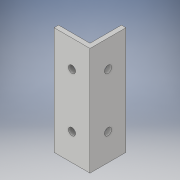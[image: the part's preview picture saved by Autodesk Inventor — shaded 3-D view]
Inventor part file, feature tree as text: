
AUTODESK INVENTOR PART (.ipt)
format: ipt  version: 2018 (Build 220112000, 112)  size: 121,344 bytes
history: native  units: in
note: dims shown in document units (in); Inventor stores cm internally (conversion verified against a paired STEP export)
features: extrude x3, sketch x3
ambient origin geometry x8: Origin, YZ Plane, XZ Plane, XY Plane, X Axis, Y Axis, Z Axis, Center Point
bodies: Solid1 (feature_tree)
feature tree (6):
  extrude  "Extrusion1"  Depth=0.125in
  extrude  "Extrusion2"  Depth=0.125in
  extrude  "Extrusion3"  Depth=1.0in
  sketch  "Sketch1"  dims[d0=1.0in d1=0.125in]
  sketch  "Sketch2"  dims[d2=1.0in d3=0.125in]
  sketch  "Sketch3"  dims[d4=3.0in d5=0.0in d6=0.5in d7=0.75in d8=0.75in d9=0.2in d10=1.0in d11=0.0in d12=0.75in d13=0.75in d14=0.2in d15=1.0in d16=0.0in]
